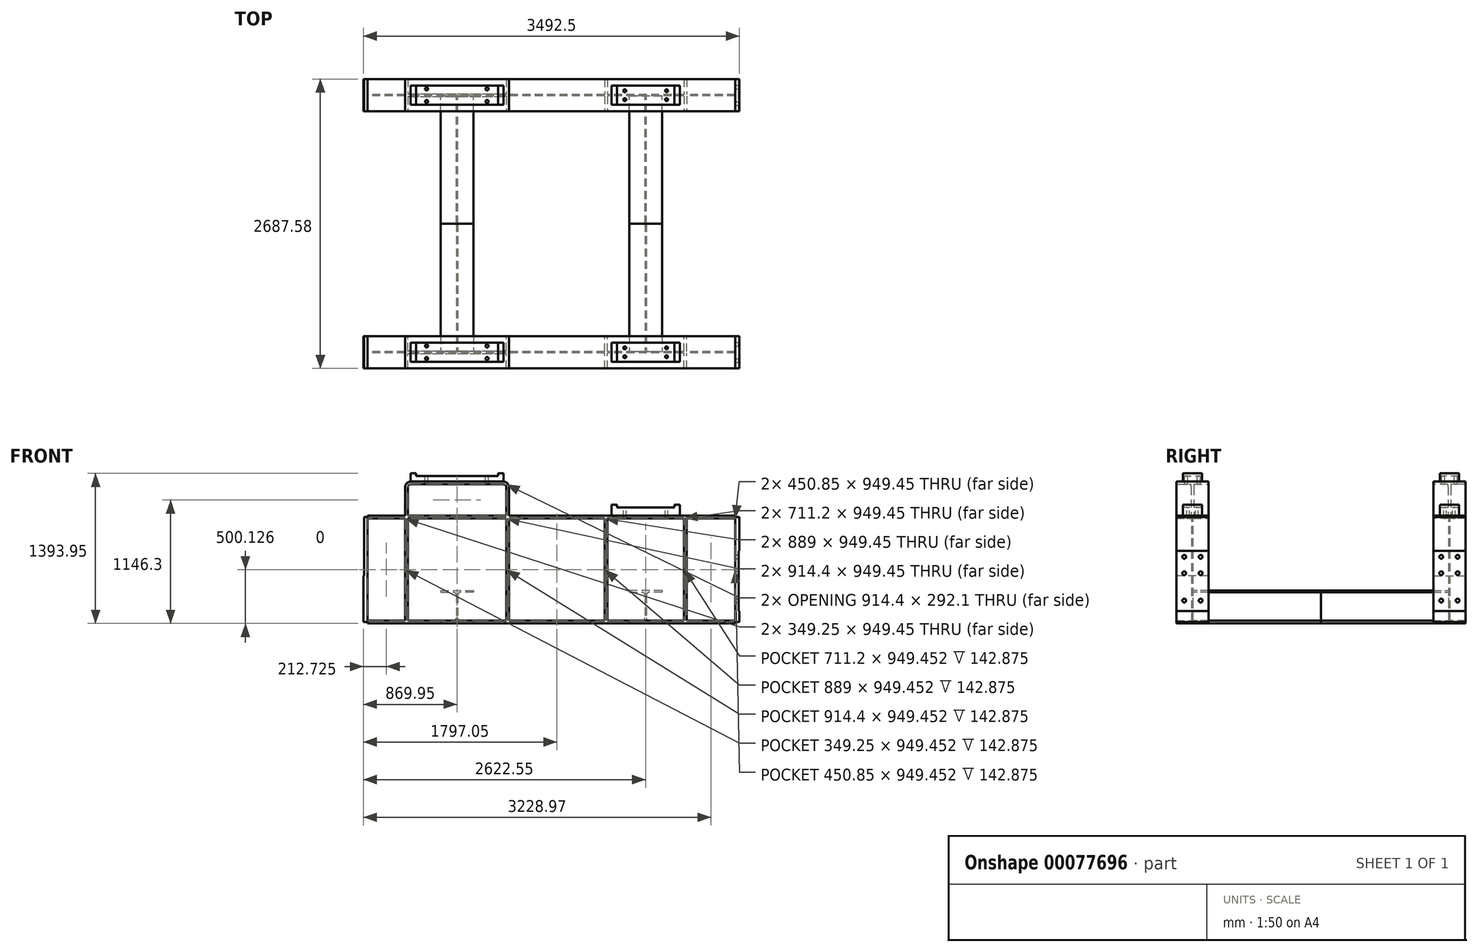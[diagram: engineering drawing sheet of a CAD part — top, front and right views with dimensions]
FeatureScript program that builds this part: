
annotation { "Feature Type Name" : "Feature", "Feature Type Description" : "" }
export const myFeature = defineFeature(function(context is Context, id is Id, definition is map)
    precondition{}
    {
        {
            var Q0;
            Q0=qCreatedBy(makeId("Front.planeOp"),FACE);
            var sketch = newSketch(context, id + "F0", { "sketchPlane" : qUnion([Q0])});
            skLineSegment(sketch, "E0.bottom", {"start": v(-1746.25, 0) * mm, "end": v(1746.25, 0) * mm});
            skLineSegment(sketch, "E0.top", {"start": v(-1746.25, 1000.25) * mm, "end": v(1746.25, 1000.25) * mm});
            skLineSegment(sketch, "E0.left", {"start": v(-1746.25, 0) * mm, "end": v(-1746.25, 1000.25) * mm});
            skLineSegment(sketch, "E0.right", {"start": v(1746.25, 0) * mm, "end": v(1746.25, 1000.25) * mm});
            skSolve(sketch);
        }
        {
            var Q0;
            Q0=qSketchRegion(id+"F0",true);
            extrude(context, id + "F1", {"entities" : qUnion([Q0]), "endBound" : BoundingType.SYMMETRIC, "depth" : 14.22 * mm});
        }
        {
            var Q0;
            Q0=qCreatedBy(makeId("Front.planeOp"),FACE);
            var sketch = newSketch(context, id + "F2", { "sketchPlane" : qUnion([Q0])});
            skLineSegment(sketch, "E1.bottom", {"start": v(-1708.15, 0) * mm, "end": v(1708.15, 0) * mm});
            skLineSegment(sketch, "E1.top", {"start": v(-1708.15, 25.4) * mm, "end": v(1708.15, 25.4) * mm});
            skLineSegment(sketch, "E1.left", {"start": v(-1708.15, 0) * mm, "end": v(-1708.15, 25.4) * mm});
            skLineSegment(sketch, "E1.right", {"start": v(1708.15, 0) * mm, "end": v(1708.15, 25.4) * mm});
            skLineSegment(sketch, "E2.0", {"start": v(1746.25, 0) * mm, "end": v(1746.25, 1000.25) * mm, "construction": true});
            skLineSegment(sketch, "E3.0", {"start": v(-1746.25, 0) * mm, "end": v(-1746.25, 1000.25) * mm, "construction": true});
            skLineSegment(sketch, "E4", {"start": v(-1746.25, 500.13) * mm, "end": v(1746.25, 500.13) * mm, "construction": true});
            skLineSegment(sketch, "E5.MirrorCS", {"start": v(1708.15, 1000.25) * mm, "end": v(1708.15, 974.85) * mm});
            skLineSegment(sketch, "E6.MirrorCS", {"start": v(-1708.15, 1000.25) * mm, "end": v(-1708.15, 974.85) * mm});
            skLineSegment(sketch, "E7.MirrorCS", {"start": v(-1708.15, 974.85) * mm, "end": v(1708.15, 974.85) * mm});
            skLineSegment(sketch, "E8.MirrorCS", {"start": v(-1708.15, 1000.25) * mm, "end": v(1708.15, 1000.25) * mm});
            skPoint(sketch, "E9.oppositeSnap0", {"position": v(-1708.15, 12.7) * mm});
            skLineSegment(sketch, "E9.bottom", {"start": v(-1708.15, 987.55) * mm, "end": v(-1746.25, 987.55) * mm});
            skLineSegment(sketch, "E9.top", {"start": v(-1708.15, 12.7) * mm, "end": v(-1746.25, 12.7) * mm});
            skLineSegment(sketch, "E9.left", {"start": v(-1708.15, 987.55) * mm, "end": v(-1708.15, 12.7) * mm});
            skLineSegment(sketch, "E9.right", {"start": v(-1746.25, 987.55) * mm, "end": v(-1746.25, 12.7) * mm});
            skLineSegment(sketch, "E10", {"start": v(0, 974.85) * mm, "end": v(0, 25.4) * mm, "construction": true});
            skLineSegment(sketch, "E11.MirrorCS", {"start": v(1708.15, 987.55) * mm, "end": v(1746.25, 987.55) * mm});
            skLineSegment(sketch, "E12.MirrorCS", {"start": v(1708.15, 12.7) * mm, "end": v(1746.25, 12.7) * mm});
            skLineSegment(sketch, "E13.MirrorCS", {"start": v(1746.25, 987.55) * mm, "end": v(1746.25, 12.7) * mm});
            skLineSegment(sketch, "E14.MirrorCS", {"start": v(1708.15, 987.55) * mm, "end": v(1708.15, 12.7) * mm});
            skPoint(sketch, "E15.MirrorP", {"position": v(1708.15, 12.7) * mm});
            skSolve(sketch);
        }
        {
            var Q0;
            Q0=qSketchRegion(id+"F2",true);
            extrude(context, id + "F3", {"entities" : qUnion([Q0]), "operationType" : NewBodyOperationType.ADD, "endBound" : BoundingType.SYMMETRIC, "depth" : 299.97 * mm});
        }
        {
            var Q0;
            Q0=qCreatedBy(makeId("Front.planeOp"),FACE);
            var sketch = newSketch(context, id + "F4", { "sketchPlane" : qUnion([Q0])});
            skPoint(sketch, "E16.0", {"position": v(-1746.25, 1000.25) * mm});
            skLineSegment(sketch, "E17.bottom", {"start": v(-1746.25, 1000.25) * mm, "end": v(-1739.9, 1000.25) * mm});
            skLineSegment(sketch, "E17.top", {"start": v(-1746.25, 441.45) * mm, "end": v(-1739.9, 441.45) * mm});
            skLineSegment(sketch, "E17.left", {"start": v(-1746.25, 1000.25) * mm, "end": v(-1746.25, 441.45) * mm});
            skLineSegment(sketch, "E17.right", {"start": v(-1739.9, 1000.25) * mm, "end": v(-1739.9, 441.45) * mm});
            skLineSegment(sketch, "E18", {"start": v(0, -58.3) * mm, "end": v(0, 1155.28) * mm, "construction": true});
            skLineSegment(sketch, "E19.MirrorCS", {"start": v(1746.25, 1000.25) * mm, "end": v(1739.9, 1000.25) * mm});
            skLineSegment(sketch, "E20.MirrorCS", {"start": v(1746.25, 441.45) * mm, "end": v(1739.9, 441.45) * mm});
            skPoint(sketch, "E21.MirrorP", {"position": v(1746.25, 1000.25) * mm});
            skLineSegment(sketch, "E22.bottom", {"start": v(1739.9, 441.45) * mm, "end": v(1766.35, 441.45) * mm});
            skLineSegment(sketch, "E22.top", {"start": v(1739.9, 114.3) * mm, "end": v(1766.35, 114.3) * mm});
            skLineSegment(sketch, "E22.left", {"start": v(1739.9, 441.45) * mm, "end": v(1739.9, 114.3) * mm});
            skLineSegment(sketch, "E22.right", {"start": v(1766.35, 441.45) * mm, "end": v(1766.35, 114.3) * mm});
            skLineSegment(sketch, "E23.top", {"start": v(1739.9, 673.1) * mm, "end": v(1766.35, 673.1) * mm});
            skLineSegment(sketch, "E23.left", {"start": v(1739.9, 441.45) * mm, "end": v(1739.9, 673.1) * mm});
            skLineSegment(sketch, "E23.right", {"start": v(1766.35, 441.45) * mm, "end": v(1766.35, 673.1) * mm});
            skSolve(sketch);
        }
        {
            var Q0;
            Q0=qSketchRegion(id+"F4",true);
            extrude(context, id + "F5", {"entities" : qUnion([Q0]), "operationType" : NewBodyOperationType.REMOVE, "endBound" : BoundingType.SYMMETRIC, "oppositeDirection" : true, "depth" : 304.8 * mm});
        }
        {
            var Q0;
            Q0=makeQuery(id+"F3.opExtrude","CAP_FACE",FACE,{"disambiguationData":[OSD([sQuery(id+"F2.wireOp",EDGE,"E1.bottom"),sQuery(id+"F2.wireOp",EDGE,"E1.top"),sQuery(id+"F2.wireOp",EDGE,"E1.left"),sQuery(id+"F2.wireOp",EDGE,"E6.MirrorCS"),sQuery(id+"F2.wireOp",EDGE,"E7.MirrorCS"),sQuery(id+"F2.wireOp",EDGE,"E8.MirrorCS"),sQuery(id+"F2.wireOp",EDGE,"E9.bottom"),sQuery(id+"F2.wireOp",EDGE,"E9.top"),sQuery(id+"F2.wireOp",EDGE,"E9.left"),sQuery(id+"F2.wireOp",EDGE,"E9.right"),sQuery(id+"F2.wireOp",EDGE,"E5.MirrorCS"),sQuery(id+"F2.wireOp",EDGE,"E1.right"),sQuery(id+"F2.wireOp",EDGE,"E11.MirrorCS"),sQuery(id+"F2.wireOp",EDGE,"E12.MirrorCS"),sQuery(id+"F2.wireOp",EDGE,"E13.MirrorCS"),sQuery(id+"F2.wireOp",EDGE,"E14.MirrorCS")])],"isStart":false});
            var sketch = newSketch(context, id + "F6", { "sketchPlane" : qUnion([Q0])});
            skLineSegment(sketch, "E24.bottom", {"start": v(-1708.15, 987.55) * mm, "end": v(-1777.82, 987.55) * mm});
            skLineSegment(sketch, "E24.top", {"start": v(-1708.15, 1019.74) * mm, "end": v(-1777.82, 1019.74) * mm});
            skLineSegment(sketch, "E24.left", {"start": v(-1708.15, 987.55) * mm, "end": v(-1708.15, 1019.74) * mm});
            skLineSegment(sketch, "E24.right", {"start": v(-1777.82, 987.55) * mm, "end": v(-1777.82, 1019.74) * mm});
            skLineSegment(sketch, "E25.bottom", {"start": v(1708.15, 987.55) * mm, "end": v(1769.2, 987.55) * mm});
            skLineSegment(sketch, "E25.top", {"start": v(1708.15, 1033.96) * mm, "end": v(1769.2, 1033.96) * mm});
            skLineSegment(sketch, "E25.left", {"start": v(1708.15, 987.55) * mm, "end": v(1708.15, 1033.96) * mm});
            skLineSegment(sketch, "E25.right", {"start": v(1769.2, 987.55) * mm, "end": v(1769.2, 1033.96) * mm});
            skLineSegment(sketch, "E26.bottom", {"start": v(1708.15, 12.7) * mm, "end": v(1775.25, 12.7) * mm});
            skLineSegment(sketch, "E26.top", {"start": v(1708.15, -29.13) * mm, "end": v(1775.25, -29.13) * mm});
            skLineSegment(sketch, "E26.left", {"start": v(1708.15, 12.7) * mm, "end": v(1708.15, -29.13) * mm});
            skLineSegment(sketch, "E26.right", {"start": v(1775.25, 12.7) * mm, "end": v(1775.25, -29.13) * mm});
            skLineSegment(sketch, "E27.bottom", {"start": v(-1708.15, 12.7) * mm, "end": v(-1780.9, 12.7) * mm});
            skLineSegment(sketch, "E27.top", {"start": v(-1708.15, -36.57) * mm, "end": v(-1780.9, -36.57) * mm});
            skLineSegment(sketch, "E27.left", {"start": v(-1708.15, 12.7) * mm, "end": v(-1708.15, -36.57) * mm});
            skLineSegment(sketch, "E27.right", {"start": v(-1780.9, 12.7) * mm, "end": v(-1780.9, -36.57) * mm});
            skSolve(sketch);
        }
        {
            var Q0;
            Q0=qSketchRegion(id+"F6",true);
            extrude(context, id + "F7", {"entities" : qUnion([Q0]), "operationType" : NewBodyOperationType.REMOVE, "endBound" : BoundingType.THROUGH_ALL, "oppositeDirection" : true, "depth" : 25.4 * mm});
        }
        {
            var Q0;
            Q0=qCreatedBy(makeId("Front.planeOp"),FACE);
            var sketch = newSketch(context, id + "F8", { "sketchPlane" : qUnion([Q0])});
            skLineSegment(sketch, "E28.0", {"start": v(-876.3, 987.55) * mm, "end": v(-876.3, 441.45) * mm, "construction": true});
            skLineSegment(sketch, "E29.0", {"start": v(876.3, 987.55) * mm, "end": v(876.3, 441.45) * mm, "construction": true});
            skLineSegment(sketch, "E30.0", {"start": v(-1708.15, 25.4) * mm, "end": v(1708.15, 25.4) * mm});
            skLineSegment(sketch, "E31.0", {"start": v(-1333.5, 1317.75) * mm, "end": v(-1333.5, 25.4) * mm});
            skLineSegment(sketch, "E32.0", {"start": v(-1358.9, 1266.95) * mm, "end": v(-1358.9, 25.4) * mm});
            skLineSegment(sketch, "E33.0", {"start": v(-1308.1, 1317.75) * mm, "end": v(-444.5, 1317.75) * mm});
            skLineSegment(sketch, "E34.0", {"start": v(-1308.1, 1292.35) * mm, "end": v(-444.5, 1292.35) * mm});
            skLineSegment(sketch, "E34.1", {"start": v(-1333.5, 1266.95) * mm, "end": v(-1333.5, 25.4) * mm});
            skLineSegment(sketch, "E35.MirrorCS", {"start": v(-419.1, 1266.95) * mm, "end": v(-419.1, 25.4) * mm});
            skLineSegment(sketch, "E36.MirrorCS", {"start": v(-393.7, 1266.95) * mm, "end": v(-393.7, 25.4) * mm});
            skLineSegment(sketch, "E37.MirrorCS", {"start": v(-419.1, 1292.35) * mm, "end": v(-419.1, 25.4) * mm});
            skPoint(sketch, "E38.visualSharp", {"position": v(-1333.5, 1292.35) * mm});
            skArc(sketch, "E38.filletArc", {"start": v(-1308.1, 1292.35) * mm, "mid": v(-1326.06, 1284.91) * mm, "end": v(-1333.5, 1266.95) * mm});
            skPoint(sketch, "E39.newPointB", {"position": v(-419.1, 1317.75) * mm});
            skArc(sketch, "E39.filletArc", {"start": v(-419.1, 1266.95) * mm, "mid": v(-426.54, 1284.91) * mm, "end": v(-444.5, 1292.35) * mm});
            skPoint(sketch, "E40.visualSharp", {"position": v(-1358.9, 1317.75) * mm});
            skArc(sketch, "E40.filletArc", {"start": v(-1308.1, 1317.75) * mm, "mid": v(-1344.02, 1302.87) * mm, "end": v(-1358.9, 1266.95) * mm});
            skPoint(sketch, "E41.visualSharp", {"position": v(-393.7, 1317.75) * mm});
            skArc(sketch, "E41.filletArc", {"start": v(-393.7, 1266.95) * mm, "mid": v(-408.58, 1302.87) * mm, "end": v(-444.5, 1317.75) * mm});
            skLineSegment(sketch, "E42", {"start": v(0, 1077.49) * mm, "end": v(0, -160.54) * mm, "construction": true});
            skLineSegment(sketch, "E43.0", {"start": v(-1708.15, 974.85) * mm, "end": v(1708.15, 974.85) * mm});
            skLineSegment(sketch, "E44.0.1", {"start": v(1708.15, 25.4) * mm, "end": v(1708.15, 974.85) * mm});
            skLineSegment(sketch, "E44.0.2", {"start": v(1708.15, 974.85) * mm, "end": v(-1708.15, 974.85) * mm});
            skLineSegment(sketch, "E44.0.3", {"start": v(-1708.15, 974.85) * mm, "end": v(-1708.15, 25.4) * mm});
            skLineSegment(sketch, "E45.0", {"start": v(520.7, 974.85) * mm, "end": v(520.7, 25.4) * mm});
            skLineSegment(sketch, "E46.0", {"start": v(495.3, 974.85) * mm, "end": v(495.3, 25.4) * mm});
            skLineSegment(sketch, "E47.MirrorCS", {"start": v(1231.9, 974.85) * mm, "end": v(1231.9, 25.4) * mm});
            skLineSegment(sketch, "E48.MirrorCS", {"start": v(1257.3, 974.85) * mm, "end": v(1257.3, 25.4) * mm});
            skSolve(sketch);
        }
        {
            var Q0;
            Q0=makeQuery(id+"F8.imprint","IMPRINT",FACE,{"disambiguationData":[TD([[makeQuery(id+"F8.imprint","IMPRINT",EDGE,{"derivedFrom":sQuery(id+"F8.wireOp",EDGE,"E34.0")}),-1.0]])]});
            extrude(context, id + "F9", {"entities" : qUnion([Q0]), "operationType" : NewBodyOperationType.ADD, "endBound" : BoundingType.SYMMETRIC, "depth" : 25.4 * mm});
        }
        {
            var Q0;
            {var subQ0=sQuery(id+"F8.wireOp",EDGE,"E40.filletArc");var subQ1=sQuery(id+"F8.wireOp",EDGE,"E32.0");var subQ2=makeQuery(id+"F8.imprint","INTERSECT",VERTEX,{"derivedFrom":[subQ1,subQ0]});Q0=makeQuery(id+"F8.imprint","IMPRINT",FACE,{"disambiguationData":[TD([[makeQuery(id+"F8.imprint","IMPRINT",EDGE,{"disambiguationData":[TD([[subQ2,-1.0]])],"derivedFrom":subQ1}),1.0]])]});}
            var Q1;
            {var subQ7=sQuery(id+"F8.wireOp",EDGE,"E33.0");Q1=makeQuery(id+"F8.imprint","IMPRINT",FACE,{"disambiguationData":[TD([[makeQuery(id+"F8.imprint","IMPRINT",EDGE,{"derivedFrom":subQ7}),-1.0]])]});}
            extrude(context, id + "F10", {"entities" : qUnion([Q0, Q1]), "operationType" : NewBodyOperationType.ADD, "endBound" : BoundingType.SYMMETRIC, "depth" : 299.97 * mm});
        }
        {
            var Q0;
            {var subQ0=sQuery(id+"F8.wireOp",EDGE,"E30.0");var subQ1=sQuery(id+"F8.wireOp",EDGE,"E32.0");var subQ2=makeQuery(id+"F8.imprint","INTERSECT",VERTEX,{"derivedFrom":[subQ1,subQ0]});Q0=makeQuery(id+"F8.imprint","IMPRINT",FACE,{"disambiguationData":[TD([[makeQuery(id+"F8.imprint","IMPRINT",EDGE,{"disambiguationData":[TD([[subQ2,1.0]])],"derivedFrom":subQ1}),1.0]])]});}
            var Q1;
            {var subQ0=sQuery(id+"F8.wireOp",EDGE,"E30.0");var subQ1=sQuery(id+"F8.wireOp",EDGE,"E36.MirrorCS");var subQ2=makeQuery(id+"F8.imprint","INTERSECT",VERTEX,{"derivedFrom":[subQ1,subQ0]});Q1=makeQuery(id+"F8.imprint","IMPRINT",FACE,{"disambiguationData":[TD([[makeQuery(id+"F8.imprint","IMPRINT",EDGE,{"disambiguationData":[TD([[subQ2,1.0]])],"derivedFrom":subQ1}),-1.0]])]});}
            var Q2;
            {var subQ0=sQuery(id+"F8.wireOp",EDGE,"E45.0");Q2=makeQuery(id+"F8.imprint","IMPRINT",FACE,{"disambiguationData":[TD([[makeQuery(id+"F8.imprint","IMPRINT",EDGE,{"derivedFrom":subQ0}),-1.0]])]});}
            var Q3;
            {var subQ0=sQuery(id+"F8.wireOp",EDGE,"E47.MirrorCS");Q3=makeQuery(id+"F8.imprint","IMPRINT",FACE,{"disambiguationData":[TD([[makeQuery(id+"F8.imprint","IMPRINT",EDGE,{"derivedFrom":subQ0}),1.0]])]});}
            extrude(context, id + "F11", {"entities" : qUnion([Q0, Q1, Q2, Q3]), "endBound" : BoundingType.SYMMETRIC, "depth" : 299.97 * mm});
        }
        {
            var Q0;
            Q0=makeQuery(id+"F1.opExtrude","SWEPT_BODY",BODY,{"disambiguationData":[OSD([sQuery(id+"F0.wireOp",EDGE,"E0.bottom"),sQuery(id+"F0.wireOp",EDGE,"E0.top"),sQuery(id+"F0.wireOp",EDGE,"E0.left"),sQuery(id+"F0.wireOp",EDGE,"E0.right")])]});
            var Q1;
            Q1=makeQuery(id+"F11.opExtrude","SWEPT_BODY",BODY,{"disambiguationData":[OSD([sQuery(id+"F8.wireOp",EDGE,"E32.0"),sQuery(id+"F8.wireOp",EDGE,"E34.1"),sQuery(id+"F8.wireOp",EDGE,"E30.0"),sQuery(id+"F8.wireOp",EDGE,"E44.0.2")])]});
            var Q2;
            Q2=makeQuery(id+"F11.opExtrude","SWEPT_BODY",BODY,{"disambiguationData":[OSD([sQuery(id+"F8.wireOp",EDGE,"E36.MirrorCS"),sQuery(id+"F8.wireOp",EDGE,"E37.MirrorCS"),sQuery(id+"F8.wireOp",EDGE,"E30.0"),sQuery(id+"F8.wireOp",EDGE,"E44.0.2")])]});
            var Q3;
            Q3=makeQuery(id+"F11.opExtrude","SWEPT_BODY",BODY,{"disambiguationData":[OSD([sQuery(id+"F8.wireOp",EDGE,"E30.0"),sQuery(id+"F8.wireOp",EDGE,"E44.0.2"),sQuery(id+"F8.wireOp",EDGE,"E45.0"),sQuery(id+"F8.wireOp",EDGE,"E46.0")])]});
            var Q4;
            Q4=makeQuery(id+"F11.opExtrude","SWEPT_BODY",BODY,{"disambiguationData":[OSD([sQuery(id+"F8.wireOp",EDGE,"E30.0"),sQuery(id+"F8.wireOp",EDGE,"E44.0.2"),sQuery(id+"F8.wireOp",EDGE,"E47.MirrorCS"),sQuery(id+"F8.wireOp",EDGE,"E48.MirrorCS")])]});
            booleanBodies(context, id + "F12", {"operationType" : BooleanOperationType.UNION, "tools" : qUnion([Q0, Q1, Q2, Q3, Q4])});
        }
        {
            var Q0;
            {var subQ11=sQuery(id+"F2.wireOp",EDGE,"E5.MirrorCS");var subQ21=sQuery(id+"F2.wireOp",EDGE,"E8.MirrorCS");Q0=makeQuery(id+"F10.boolean.opBoolean","SPLIT",FACE,{"disambiguationData":[TD([makeQuery(id+"F3.opExtrude","SWEPT_FACE",FACE,{"disambiguationData":[OSD([subQ11])]})])],"derivedFrom":makeQuery(id+"F3.boolean.opBoolean","MERGE",FACE,{"derivedFrom":[makeQuery(id+"F1.opExtrude","SWEPT_FACE",FACE,{"disambiguationData":[OSD([sQuery(id+"F0.wireOp",EDGE,"E0.top")])]}),makeQuery(id+"F3.opExtrude","SWEPT_FACE",FACE,{"disambiguationData":[OSD([subQ21])]})]})});}
            var sketch = newSketch(context, id + "F13", { "sketchPlane" : qUnion([Q0])});
            skLineSegment(sketch, "E49.0", {"start": v(1739.9, 149.99) * mm, "end": v(1739.9, -149.99) * mm, "construction": true});
            skLineSegment(sketch, "E50.0", {"start": v(876.3, 149.99) * mm, "end": v(876.3, -149.99) * mm, "construction": true});
            skLineSegment(sketch, "E51", {"start": v(1921.42, 0) * mm, "end": v(-99.23, 0) * mm, "construction": true});
            skPoint(sketch, "E51.endSnap0", {"position": v(1708.15, 0) * mm});
            skLineSegment(sketch, "E52.0", {"start": v(1193.8, 88.9) * mm, "end": v(1193.8, -88.9) * mm});
            skLineSegment(sketch, "E53.0", {"start": v(558.8, 88.9) * mm, "end": v(558.8, -88.9) * mm});
            skLineSegment(sketch, "E54.0", {"start": v(1193.8, 88.9) * mm, "end": v(558.8, 88.9) * mm});
            skLineSegment(sketch, "E55.trimOffspring", {"start": v(1193.8, -88.9) * mm, "end": v(558.8, -88.9) * mm});
            skSolve(sketch);
        }
        {
            var Q0;
            Q0 = qSketchRegion(id + "F13", true);
            extrude(context, id + "F14", {"entities" : qUnion([Q0]), "operationType" : NewBodyOperationType.ADD, "depth" : 76.2 * mm});
        }
        {
            var Q0;
            Q0=makeQuery(id+"F14.opExtrude","CAP_FACE",FACE,{"disambiguationData":[OSD([sQuery(id+"F13.wireOp",EDGE,"E52.0"),sQuery(id+"F13.wireOp",EDGE,"E53.0"),sQuery(id+"F13.wireOp",EDGE,"E54.0"),sQuery(id+"F13.wireOp",EDGE,"E55.trimOffspring")])],"isStart":false});
            var sketch = newSketch(context, id + "F15", { "sketchPlane" : qUnion([Q0])});
            skLineSegment(sketch, "E56", {"start": v(876.3, 88.9) * mm, "end": v(876.3, -88.9) * mm, "construction": true});
            skLineSegment(sketch, "E57.0", {"start": v(1143, 88.9) * mm, "end": v(1143, -88.9) * mm, "construction": true});
            skLineSegment(sketch, "E58.bottom", {"start": v(1143, 88.9) * mm, "end": v(1193.8, 88.9) * mm});
            skLineSegment(sketch, "E58.top", {"start": v(1143, -88.9) * mm, "end": v(1193.8, -88.9) * mm});
            skLineSegment(sketch, "E58.left", {"start": v(1143, 88.9) * mm, "end": v(1143, -88.9) * mm});
            skLineSegment(sketch, "E58.right", {"start": v(1193.8, 88.9) * mm, "end": v(1193.8, -88.9) * mm});
            skLineSegment(sketch, "E59.MirrorCS", {"start": v(609.6, 88.9) * mm, "end": v(609.6, -88.9) * mm, "construction": true});
            skLineSegment(sketch, "E60.MirrorCS", {"start": v(558.8, 88.9) * mm, "end": v(558.8, -88.9) * mm});
            skLineSegment(sketch, "E61.MirrorCS", {"start": v(609.6, 88.9) * mm, "end": v(609.6, -88.9) * mm});
            skLineSegment(sketch, "E62.MirrorCS", {"start": v(609.6, -88.9) * mm, "end": v(558.8, -88.9) * mm});
            skLineSegment(sketch, "E63.MirrorCS", {"start": v(609.6, 88.9) * mm, "end": v(558.8, 88.9) * mm});
            skSolve(sketch);
        }
        {
            var Q0;
            Q0 = qSketchRegion(id + "F15", true);
            extrude(context, id + "F16", {"entities" : qUnion([Q0]), "operationType" : NewBodyOperationType.ADD, "depth" : 25.4 * mm});
        }
        {
            var Q0;
            Q0=makeQuery(id+"F14.opExtrude","CAP_FACE",FACE,{"disambiguationData":[OSD([sQuery(id+"F13.wireOp",EDGE,"E52.0"),sQuery(id+"F13.wireOp",EDGE,"E53.0"),sQuery(id+"F13.wireOp",EDGE,"E54.0"),sQuery(id+"F13.wireOp",EDGE,"E55.trimOffspring")])],"isStart":false});
            var sketch = newSketch(context, id + "F17", { "sketchPlane" : qUnion([Q0])});
            skLineSegment(sketch, "E64", {"start": v(876.3, 88.9) * mm, "end": v(876.3, -88.9) * mm, "construction": true});
            skLineSegment(sketch, "E65", {"start": v(609.6, 0) * mm, "end": v(1143, 0) * mm, "construction": true});
            skLineSegment(sketch, "E66.0", {"start": v(1070.86, 88.9) * mm, "end": v(1070.86, -88.9) * mm, "construction": true});
            skLineSegment(sketch, "E67.0", {"start": v(609.6, 41.15) * mm, "end": v(1143, 41.15) * mm, "construction": true});
            skLineSegment(sketch, "E68.0", {"start": v(609.6, -41.15) * mm, "end": v(1143, -41.15) * mm, "construction": true});
            skLineSegment(sketch, "E69.0", {"start": v(682, 88.9) * mm, "end": v(682, -88.9) * mm, "construction": true});
            skPoint(sketch, "E70", {"position": v(682, 41.15) * mm});
            skPoint(sketch, "E71", {"position": v(682, -41.15) * mm});
            skPoint(sketch, "E72", {"position": v(1070.86, 41.15) * mm});
            skPoint(sketch, "E73", {"position": v(1070.86, -41.15) * mm});
            skSolve(sketch);
        }
        {
            var Q0;
            Q0=sQuery(id+"F17.wireOp",VERTEX,"E70");
            var Q1;
            Q1=sQuery(id+"F17.wireOp",VERTEX,"E72");
            var Q2;
            Q2=sQuery(id+"F17.wireOp",VERTEX,"E73");
            var Q3;
            Q3=sQuery(id+"F17.wireOp",VERTEX,"E71");
            var Q4;
            Q4=makeQuery(id+"F1.opExtrude","SWEPT_BODY",BODY,{"disambiguationData":[OSD([sQuery(id+"F0.wireOp",EDGE,"E0.bottom"),sQuery(id+"F0.wireOp",EDGE,"E0.top"),sQuery(id+"F0.wireOp",EDGE,"E0.left"),sQuery(id+"F0.wireOp",EDGE,"E0.right")])]});
            hole(context, id + "F18", {"style" : HoleStyle.SIMPLE, "endStyle" : HoleEndStyle.BLIND, "standardTappedOrClearance" : lookupTablePath({ "standard" : "ANSI", "fit" : "Normal (ASME)", "size" : "1", "type" : "Clearance" }), "standardBlindInLast" : lookupTablePath({ "fit" : "Free", "standard" : "ANSI", "size" : "1", "type" : "Clearance" }), "holeDiameter" : 26.2 * mm, "holeDepth" : 101.6 * mm, "locations" : qUnion([Q0, Q1, Q2, Q3]), "scope" : qUnion([Q4])});
        }
        {
            var Q0;
            Q0=makeQuery(id+"F5.boolean.opBoolean","COPY",FACE,{"derivedFrom":makeQuery(id+"F5.opExtrude","SWEPT_FACE",FACE,{"disambiguationData":[OSD([sQuery(id+"F4.wireOp",EDGE,"E22.left"),sQuery(id+"F4.wireOp",EDGE,"E23.left")])]})});
            var sketch = newSketch(context, id + "F19", { "sketchPlane" : qUnion([Q0])});
            skLineSegment(sketch, "E74.0", {"start": v(88.9, 1076.45) * mm, "end": v(-88.9, 1076.45) * mm, "construction": true});
            skLineSegment(sketch, "E75.0", {"start": v(88.9, 619.25) * mm, "end": v(-88.9, 619.25) * mm, "construction": true});
            skLineSegment(sketch, "E76.0", {"start": v(88.9, 466.85) * mm, "end": v(-88.9, 466.85) * mm, "construction": true});
            skLineSegment(sketch, "E77.0", {"start": v(88.9, 212.85) * mm, "end": v(-88.9, 212.85) * mm, "construction": true});
            skLineSegment(sketch, "E78", {"start": v(0, -74.03) * mm, "end": v(0, 756.57) * mm, "construction": true});
            skPoint(sketch, "E78.endSnap0", {"position": v(0, 673.1) * mm});
            skLineSegment(sketch, "E79.0", {"start": v(-76.2, -74.03) * mm, "end": v(-76.2, 756.57) * mm, "construction": true});
            skPoint(sketch, "E80", {"position": v(-76.2, 619.25) * mm});
            skPoint(sketch, "E81", {"position": v(-76.2, 466.85) * mm});
            skPoint(sketch, "E82", {"position": v(-76.2, 212.85) * mm});
            skPoint(sketch, "E83.MirrorP", {"position": v(76.2, 619.25) * mm});
            skPoint(sketch, "E84.MirrorP", {"position": v(76.2, 466.85) * mm});
            skPoint(sketch, "E85.MirrorP", {"position": v(76.2, 212.85) * mm});
            skSolve(sketch);
        }
        {
            var Q0;
            Q0=sQuery(id+"F19.wireOp",VERTEX,"E80");
            var Q1;
            Q1=sQuery(id+"F19.wireOp",VERTEX,"E83.MirrorP");
            var Q2;
            Q2=sQuery(id+"F19.wireOp",VERTEX,"E84.MirrorP");
            var Q3;
            Q3=sQuery(id+"F19.wireOp",VERTEX,"E81");
            var Q4;
            Q4=sQuery(id+"F19.wireOp",VERTEX,"E85.MirrorP");
            var Q5;
            Q5=sQuery(id+"F19.wireOp",VERTEX,"E82");
            var Q6;
            Q6=makeQuery(id+"F1.opExtrude","SWEPT_BODY",BODY,{"disambiguationData":[OSD([sQuery(id+"F0.wireOp",EDGE,"E0.bottom"),sQuery(id+"F0.wireOp",EDGE,"E0.top"),sQuery(id+"F0.wireOp",EDGE,"E0.left"),sQuery(id+"F0.wireOp",EDGE,"E0.right")])]});
            hole(context, id + "F20", {"style" : HoleStyle.SIMPLE, "endStyle" : HoleEndStyle.BLIND, "holeDiameter" : 35.05 * mm, "holeDepth" : 101.6 * mm, "locations" : qUnion([Q0, Q1, Q2, Q3, Q4, Q5]), "scope" : qUnion([Q6])});
        }
        {
            var Q0;
            Q0=makeQuery(id+"F10.opExtrude","SWEPT_FACE",FACE,{"disambiguationData":[OSD([sQuery(id+"F8.wireOp",EDGE,"E33.0")])]});
            var sketch = newSketch(context, id + "F21", { "sketchPlane" : qUnion([Q0])});
            skLineSegment(sketch, "E86.0", {"start": v(1143, 88.9) * mm, "end": v(609.6, 88.9) * mm, "construction": true});
            skLineSegment(sketch, "E87", {"start": v(876.3, 88.9) * mm, "end": v(876.3, -517.5) * mm, "construction": true});
            skLineSegment(sketch, "E88.0", {"start": v(-876.3, 88.9) * mm, "end": v(-876.3, -517.5) * mm, "construction": true});
            skLineSegment(sketch, "E89", {"start": v(-1945.55, 0) * mm, "end": v(-145.35, 0) * mm, "construction": true});
            skLineSegment(sketch, "E90.0", {"start": v(-1308.1, 88.9) * mm, "end": v(-1308.1, -517.5) * mm, "construction": true});
            skLineSegment(sketch, "E91.0", {"start": v(-1945.55, -88.9) * mm, "end": v(-145.35, -88.9) * mm, "construction": true});
            skLineSegment(sketch, "E92.bottom", {"start": v(-1308.1, -88.9) * mm, "end": v(-444.5, -88.9) * mm});
            skLineSegment(sketch, "E92.top", {"start": v(-1308.1, 88.9) * mm, "end": v(-444.5, 88.9) * mm});
            skLineSegment(sketch, "E92.left", {"start": v(-1308.1, -88.9) * mm, "end": v(-1308.1, 88.9) * mm});
            skLineSegment(sketch, "E92.right", {"start": v(-444.5, -88.9) * mm, "end": v(-444.5, 88.9) * mm});
            skSolve(sketch);
        }
        {
            var Q0;
            Q0 = qSketchRegion(id + "F21", true);
            extrude(context, id + "F22", {"entities" : qUnion([Q0]), "operationType" : NewBodyOperationType.ADD, "depth" : 76.2 * mm});
        }
        {
            var Q0;
            Q0=makeQuery(id+"F22.opExtrude","CAP_FACE",FACE,{"disambiguationData":[OSD([sQuery(id+"F21.wireOp",EDGE,"E92.bottom"),sQuery(id+"F21.wireOp",EDGE,"E92.top"),sQuery(id+"F21.wireOp",EDGE,"E92.left"),sQuery(id+"F21.wireOp",EDGE,"E92.right")])],"isStart":false});
            var sketch = newSketch(context, id + "F23", { "sketchPlane" : qUnion([Q0])});
            skLineSegment(sketch, "E93.0", {"start": v(-495.3, -88.9) * mm, "end": v(-495.3, 88.9) * mm});
            skLineSegment(sketch, "E94.0", {"start": v(-1257.3, -88.9) * mm, "end": v(-1257.3, 88.9) * mm});
            skLineSegment(sketch, "E95.0", {"start": v(-1308.1, 88.9) * mm, "end": v(-444.5, 88.9) * mm});
            skLineSegment(sketch, "E96.0", {"start": v(-1308.1, -88.9) * mm, "end": v(-444.5, -88.9) * mm});
            skSolve(sketch);
        }
        {
            var Q0;
            Q0 = qSketchRegion(id + "F23", true);
            extrude(context, id + "F24", {"entities" : qUnion([Q0]), "operationType" : NewBodyOperationType.REMOVE, "oppositeDirection" : true, "depth" : 25.4 * mm});
        }
        {
            var Q0;
            Q0=makeQuery(id+"F24.boolean.opBoolean","COPY",FACE,{"derivedFrom":makeQuery(id+"F24.opExtrude","CAP_FACE",FACE,{"disambiguationData":[OSD([sQuery(id+"F23.wireOp",EDGE,"E93.0"),sQuery(id+"F23.wireOp",EDGE,"E94.0"),sQuery(id+"F23.wireOp",EDGE,"E95.0"),sQuery(id+"F23.wireOp",EDGE,"E96.0")])],"isStart":false})});
            var sketch = newSketch(context, id + "F25", { "sketchPlane" : qUnion([Q0])});
            skLineSegment(sketch, "E97", {"start": v(-495.3, 0) * mm, "end": v(-1257.3, 0) * mm, "construction": true});
            skLineSegment(sketch, "E98", {"start": v(-876.3, 88.9) * mm, "end": v(-876.3, -88.9) * mm, "construction": true});
            skLineSegment(sketch, "E99.0", {"start": v(-495.3, 58.67) * mm, "end": v(-1257.3, 58.67) * mm, "construction": true});
            skLineSegment(sketch, "E100.0", {"start": v(-1158.75, 88.9) * mm, "end": v(-1158.75, -88.9) * mm, "construction": true});
            skLineSegment(sketch, "E101.0", {"start": v(-596.9, 88.9) * mm, "end": v(-596.9, -88.9) * mm, "construction": true});
            skPoint(sketch, "E102", {"position": v(-1158.75, 58.67) * mm});
            skPoint(sketch, "E103", {"position": v(-596.9, 58.67) * mm});
            skPoint(sketch, "E104.MirrorP", {"position": v(-1158.75, -58.67) * mm});
            skPoint(sketch, "E105.MirrorP", {"position": v(-596.9, -58.67) * mm});
            skSolve(sketch);
        }
        {
            var Q0;
            Q0=sQuery(id+"F25.wireOp",VERTEX,"E102");
            var Q1;
            Q1=sQuery(id+"F25.wireOp",VERTEX,"E104.MirrorP");
            var Q2;
            Q2=sQuery(id+"F25.wireOp",VERTEX,"E103");
            var Q3;
            Q3=sQuery(id+"F25.wireOp",VERTEX,"E105.MirrorP");
            var Q4;
            Q4=makeQuery(id+"F1.opExtrude","SWEPT_BODY",BODY,{"disambiguationData":[OSD([sQuery(id+"F0.wireOp",EDGE,"E0.bottom"),sQuery(id+"F0.wireOp",EDGE,"E0.top"),sQuery(id+"F0.wireOp",EDGE,"E0.left"),sQuery(id+"F0.wireOp",EDGE,"E0.right")])]});
            hole(context, id + "F26", {"style" : HoleStyle.SIMPLE, "endStyle" : HoleEndStyle.BLIND, "holeDiameter" : 28.57 * mm, "holeDepth" : 101.6 * mm, "locations" : qUnion([Q0, Q1, Q2, Q3]), "scope" : qUnion([Q4])});
        }
        {
            var Q0;
            {var subQ0=makeQuery(id+"F3.opExtrude","SWEPT_FACE",FACE,{"disambiguationData":[OSD([sQuery(id+"F2.wireOp",EDGE,"E1.top")])]});Q0=makeQuery(id+"F12.opBoolean","SPLIT",FACE,{"disambiguationData":[TD([makeQuery(id+"F11.opExtrude","SWEPT_FACE",FACE,{"disambiguationData":[OSD([sQuery(id+"F8.wireOp",EDGE,"E45.0")])]})])],"derivedFrom":makeQuery(id+"F3.boolean.opBoolean","SPLIT",FACE,{"disambiguationData":[TD([subQ0])],"derivedFrom":makeQuery(id+"F1.opExtrude","CAP_FACE",FACE,{"disambiguationData":[OSD([sQuery(id+"F0.wireOp",EDGE,"E0.bottom"),sQuery(id+"F0.wireOp",EDGE,"E0.top"),sQuery(id+"F0.wireOp",EDGE,"E0.left"),sQuery(id+"F0.wireOp",EDGE,"E0.right")])],"isStart":true})})});}
            var sketch = newSketch(context, id + "F27", { "sketchPlane" : qUnion([Q0])});
            skLineSegment(sketch, "E106.0", {"start": v(-1143, 1076.45) * mm, "end": v(-609.6, 1076.45) * mm, "construction": true});
            skLineSegment(sketch, "E107.0", {"start": v(1257.3, 1368.55) * mm, "end": v(495.3, 1368.55) * mm, "construction": true});
            skLineSegment(sketch, "E108", {"start": v(-876.3, 1076.45) * mm, "end": v(-876.3, 0) * mm, "construction": true});
            skPoint(sketch, "E108.endSnap0", {"position": v(-876.3, 25.4) * mm});
            skLineSegment(sketch, "E109", {"start": v(876.3, 1368.55) * mm, "end": v(876.3, 0) * mm, "construction": true});
            skPoint(sketch, "E109.endSnap0", {"position": v(876.3, 1368.55) * mm});
            skLineSegment(sketch, "E110.0", {"start": v(1708.15, 0) * mm, "end": v(-1708.15, 0) * mm, "construction": true});
            skPoint(sketch, "E111.orphan", {"position": v(-876.3, -88.01) * mm});
            skPoint(sketch, "E112.orphan", {"position": v(876.3, -147.03) * mm});
            skLineSegment(sketch, "E113", {"start": v(-876.3, 0) * mm, "end": v(-1028.7, 0) * mm});
            skLineSegment(sketch, "E114", {"start": v(-1028.7, 0) * mm, "end": v(-1028.7, 25.4) * mm});
            skLineSegment(sketch, "E115", {"start": v(-1015.77, 25.4) * mm, "end": v(-909.32, 25.4) * mm});
            skLineSegment(sketch, "E116", {"start": v(-883.92, 50.8) * mm, "end": v(-883.92, 264.03) * mm});
            skLineSegment(sketch, "E117", {"start": v(-909.32, 289.43) * mm, "end": v(-1028.7, 289.43) * mm});
            skLineSegment(sketch, "E118", {"start": v(-1028.7, 289.43) * mm, "end": v(-1028.7, 304.8) * mm});
            skLineSegment(sketch, "E119", {"start": v(-1028.7, 304.8) * mm, "end": v(-876.3, 304.8) * mm});
            skPoint(sketch, "E120.visualSharp", {"position": v(-883.92, 289.43) * mm});
            skArc(sketch, "E120.filletArc", {"start": v(-883.92, 264.03) * mm, "mid": v(-891.36, 282) * mm, "end": v(-909.32, 289.43) * mm});
            skPoint(sketch, "E121.visualSharp", {"position": v(-883.92, 25.4) * mm});
            skArc(sketch, "E121.filletArc", {"start": v(-909.32, 25.4) * mm, "mid": v(-891.36, 32.84) * mm, "end": v(-883.92, 50.8) * mm});
            skLineSegment(sketch, "E122.MirrorCS", {"start": v(-723.9, 289.43) * mm, "end": v(-723.9, 304.8) * mm});
            skLineSegment(sketch, "E123.MirrorCS", {"start": v(-723.9, 0) * mm, "end": v(-723.9, 25.4) * mm});
            skArc(sketch, "E124.MirrorCS", {"start": v(-843.28, 25.4) * mm, "mid": v(-861.24, 32.84) * mm, "end": v(-868.68, 50.8) * mm});
            skArc(sketch, "E125.MirrorCS", {"start": v(-868.68, 264.03) * mm, "mid": v(-861.24, 282) * mm, "end": v(-843.28, 289.43) * mm});
            skLineSegment(sketch, "E126.MirrorCS", {"start": v(-736.83, 25.4) * mm, "end": v(-843.28, 25.4) * mm});
            skLineSegment(sketch, "E127.MirrorCS", {"start": v(-868.68, 50.8) * mm, "end": v(-868.68, 264.03) * mm});
            skLineSegment(sketch, "E128.MirrorCS", {"start": v(-876.3, 0) * mm, "end": v(-723.9, 0) * mm});
            skLineSegment(sketch, "E129.MirrorCS", {"start": v(-843.28, 289.43) * mm, "end": v(-723.9, 289.43) * mm});
            skPoint(sketch, "E130.MirrorP", {"position": v(-868.68, 25.4) * mm});
            skLineSegment(sketch, "E131.MirrorCS", {"start": v(-723.9, 304.8) * mm, "end": v(-876.3, 304.8) * mm});
            skPoint(sketch, "E132.MirrorP", {"position": v(-868.68, 289.43) * mm});
            skLineSegment(sketch, "E133", {"start": v(-876.3, 709.43) * mm, "end": v(876.3, 709.43) * mm, "construction": true});
            skLineSegment(sketch, "E134", {"start": v(0, 709.43) * mm, "end": v(0, 444.83) * mm, "construction": true});
            skArc(sketch, "E135.MirrorCS", {"start": v(909.32, 25.4) * mm, "mid": v(891.36, 32.84) * mm, "end": v(883.92, 50.8) * mm});
            skArc(sketch, "E136.MirrorCS", {"start": v(868.68, 264.03) * mm, "mid": v(861.24, 282) * mm, "end": v(843.28, 289.43) * mm});
            skArc(sketch, "E137.MirrorCS", {"start": v(843.28, 25.4) * mm, "mid": v(861.24, 32.84) * mm, "end": v(868.68, 50.8) * mm});
            skArc(sketch, "E138.MirrorCS", {"start": v(883.92, 264.03) * mm, "mid": v(891.36, 282) * mm, "end": v(909.32, 289.43) * mm});
            skLineSegment(sketch, "E139.MirrorCS", {"start": v(723.9, 0) * mm, "end": v(723.9, 25.4) * mm});
            skLineSegment(sketch, "E140.MirrorCS", {"start": v(723.9, 289.43) * mm, "end": v(723.9, 304.8) * mm});
            skLineSegment(sketch, "E141.MirrorCS", {"start": v(1028.7, 289.43) * mm, "end": v(1028.7, 304.8) * mm});
            skLineSegment(sketch, "E142.MirrorCS", {"start": v(1028.7, 0) * mm, "end": v(1028.7, 25.4) * mm});
            skPoint(sketch, "E143.MirrorP", {"position": v(876.3, 25.4) * mm});
            skPoint(sketch, "E144.MirrorP", {"position": v(876.3, -88.01) * mm});
            skPoint(sketch, "E145.MirrorP", {"position": v(868.68, 25.4) * mm});
            skPoint(sketch, "E146.MirrorP", {"position": v(883.92, 289.43) * mm});
            skLineSegment(sketch, "E147.MirrorCS", {"start": v(876.3, 0) * mm, "end": v(723.9, 0) * mm});
            skLineSegment(sketch, "E148.MirrorCS", {"start": v(723.9, 304.8) * mm, "end": v(876.3, 304.8) * mm});
            skPoint(sketch, "E149.MirrorP", {"position": v(883.92, 25.4) * mm});
            skLineSegment(sketch, "E150.MirrorCS", {"start": v(1015.77, 25.4) * mm, "end": v(909.32, 25.4) * mm});
            skPoint(sketch, "E151.MirrorP", {"position": v(868.68, 289.43) * mm});
            skLineSegment(sketch, "E152.MirrorCS", {"start": v(736.83, 25.4) * mm, "end": v(843.28, 25.4) * mm});
            skLineSegment(sketch, "E153.MirrorCS", {"start": v(883.92, 50.8) * mm, "end": v(883.92, 264.03) * mm});
            skLineSegment(sketch, "E154.MirrorCS", {"start": v(876.3, 0) * mm, "end": v(1028.7, 0) * mm});
            skLineSegment(sketch, "E155.MirrorCS", {"start": v(909.32, 289.43) * mm, "end": v(1028.7, 289.43) * mm});
            skLineSegment(sketch, "E156.MirrorCS", {"start": v(868.68, 50.8) * mm, "end": v(868.68, 264.03) * mm});
            skLineSegment(sketch, "E157.MirrorCS", {"start": v(843.28, 289.43) * mm, "end": v(723.9, 289.43) * mm});
            skLineSegment(sketch, "E158.MirrorCS", {"start": v(1028.7, 304.8) * mm, "end": v(876.3, 304.8) * mm});
            skSolve(sketch);
        }
        {
            var Q0;
            Q0=qCreatedBy(makeId("Front.planeOp"),FACE);
            cPlane(context, id + "F28", {"entities" : qUnion([Q0]), "cplaneType" : CPlaneType.OFFSET, "offset" : 1193.8 * mm, "oppositeDirection" : true, "width" : 152.4 * mm, "height" : 152.4 * mm});
        }
        {
            var Q0;
            Q0=makeQuery(id+"F27.imprint","IMPRINT",FACE,{"disambiguationData":[TD([[makeQuery(id+"F27.imprint","IMPRINT",EDGE,{"derivedFrom":sQuery(id+"F27.wireOp",EDGE,"E116")}),-1.0]])]});
            var Q1;
            Q1=makeQuery(id+"F27.imprint","IMPRINT",FACE,{"disambiguationData":[TD([[makeQuery(id+"F27.imprint","IMPRINT",EDGE,{"derivedFrom":sQuery(id+"F27.wireOp",EDGE,"E113")}),-1.0]])]});
            var Q2;
            Q2=qCreatedBy(id+"F28.planeOp",FACE);
            extrude(context, id + "F29", {"entities" : qUnion([Q0, Q1]), "endBound" : BoundingType.UP_TO_SURFACE, "endBoundEntityFace" : qUnion([Q2]), "depth" : 25.4 * mm});
        }
        {
            var Q0;
            Q0=makeQuery(id+"F29.opExtrude","SWEPT_BODY",BODY,{"disambiguationData":[OSD([sQuery(id+"F0.wireOp",EDGE,"E0.bottom"),sQuery(id+"F0.wireOp",EDGE,"E0.top"),sQuery(id+"F0.wireOp",EDGE,"E0.left"),sQuery(id+"F0.wireOp",EDGE,"E0.right"),sQuery(id+"F2.wireOp",EDGE,"E1.top"),sQuery(id+"F27.wireOp",EDGE,"E113"),sQuery(id+"F27.wireOp",EDGE,"E114"),sQuery(id+"F27.wireOp",EDGE,"E115"),sQuery(id+"F27.wireOp",EDGE,"E116"),sQuery(id+"F27.wireOp",EDGE,"E117"),sQuery(id+"F27.wireOp",EDGE,"E118"),sQuery(id+"F27.wireOp",EDGE,"E119"),sQuery(id+"F27.wireOp",EDGE,"E120.filletArc"),sQuery(id+"F27.wireOp",EDGE,"E121.filletArc"),sQuery(id+"F27.wireOp",EDGE,"E122.MirrorCS"),sQuery(id+"F27.wireOp",EDGE,"E123.MirrorCS"),sQuery(id+"F27.wireOp",EDGE,"E124.MirrorCS"),sQuery(id+"F27.wireOp",EDGE,"E125.MirrorCS"),sQuery(id+"F27.wireOp",EDGE,"E126.MirrorCS"),sQuery(id+"F27.wireOp",EDGE,"E127.MirrorCS"),sQuery(id+"F27.wireOp",EDGE,"E128.MirrorCS"),sQuery(id+"F27.wireOp",EDGE,"E129.MirrorCS"),sQuery(id+"F27.wireOp",EDGE,"E131.MirrorCS")])]});
            var Q1;
            Q1=qCreatedBy(makeId("Right.planeOp"),FACE);
            mirror(context, id + "F30", {"entities" : qUnion([Q0]), "mirrorPlane" : qUnion([Q1])});
        }
        {
            var Q0;
            Q0=makeQuery(id+"F1.opExtrude","SWEPT_BODY",BODY,{"disambiguationData":[OSD([sQuery(id+"F0.wireOp",EDGE,"E0.bottom"),sQuery(id+"F0.wireOp",EDGE,"E0.top"),sQuery(id+"F0.wireOp",EDGE,"E0.left"),sQuery(id+"F0.wireOp",EDGE,"E0.right")])]});
            var Q1;
            Q1=makeQuery(id+"F29.opExtrude","SWEPT_BODY",BODY,{"disambiguationData":[OSD([sQuery(id+"F0.wireOp",EDGE,"E0.bottom"),sQuery(id+"F0.wireOp",EDGE,"E0.top"),sQuery(id+"F0.wireOp",EDGE,"E0.left"),sQuery(id+"F0.wireOp",EDGE,"E0.right"),sQuery(id+"F2.wireOp",EDGE,"E1.top"),sQuery(id+"F27.wireOp",EDGE,"E113"),sQuery(id+"F27.wireOp",EDGE,"E114"),sQuery(id+"F27.wireOp",EDGE,"E115"),sQuery(id+"F27.wireOp",EDGE,"E116"),sQuery(id+"F27.wireOp",EDGE,"E117"),sQuery(id+"F27.wireOp",EDGE,"E118"),sQuery(id+"F27.wireOp",EDGE,"E119"),sQuery(id+"F27.wireOp",EDGE,"E120.filletArc"),sQuery(id+"F27.wireOp",EDGE,"E121.filletArc"),sQuery(id+"F27.wireOp",EDGE,"E122.MirrorCS"),sQuery(id+"F27.wireOp",EDGE,"E123.MirrorCS"),sQuery(id+"F27.wireOp",EDGE,"E124.MirrorCS"),sQuery(id+"F27.wireOp",EDGE,"E125.MirrorCS"),sQuery(id+"F27.wireOp",EDGE,"E126.MirrorCS"),sQuery(id+"F27.wireOp",EDGE,"E127.MirrorCS"),sQuery(id+"F27.wireOp",EDGE,"E128.MirrorCS"),sQuery(id+"F27.wireOp",EDGE,"E129.MirrorCS"),sQuery(id+"F27.wireOp",EDGE,"E131.MirrorCS")])]});
            var Q2;
            Q2=makeQuery(id+"F30.opPattern","COPY",BODY,{"derivedFrom":makeQuery(id+"F29.opExtrude","SWEPT_BODY",BODY,{"disambiguationData":[OSD([sQuery(id+"F0.wireOp",EDGE,"E0.bottom"),sQuery(id+"F0.wireOp",EDGE,"E0.top"),sQuery(id+"F0.wireOp",EDGE,"E0.left"),sQuery(id+"F0.wireOp",EDGE,"E0.right"),sQuery(id+"F2.wireOp",EDGE,"E1.top"),sQuery(id+"F27.wireOp",EDGE,"E113"),sQuery(id+"F27.wireOp",EDGE,"E114"),sQuery(id+"F27.wireOp",EDGE,"E115"),sQuery(id+"F27.wireOp",EDGE,"E116"),sQuery(id+"F27.wireOp",EDGE,"E117"),sQuery(id+"F27.wireOp",EDGE,"E118"),sQuery(id+"F27.wireOp",EDGE,"E119"),sQuery(id+"F27.wireOp",EDGE,"E120.filletArc"),sQuery(id+"F27.wireOp",EDGE,"E121.filletArc"),sQuery(id+"F27.wireOp",EDGE,"E122.MirrorCS"),sQuery(id+"F27.wireOp",EDGE,"E123.MirrorCS"),sQuery(id+"F27.wireOp",EDGE,"E124.MirrorCS"),sQuery(id+"F27.wireOp",EDGE,"E125.MirrorCS"),sQuery(id+"F27.wireOp",EDGE,"E126.MirrorCS"),sQuery(id+"F27.wireOp",EDGE,"E127.MirrorCS"),sQuery(id+"F27.wireOp",EDGE,"E128.MirrorCS"),sQuery(id+"F27.wireOp",EDGE,"E129.MirrorCS"),sQuery(id+"F27.wireOp",EDGE,"E131.MirrorCS")])]}),"instanceName":"1"});
            var Q3;
            Q3=qCreatedBy(id+"F28.planeOp",FACE);
            mirror(context, id + "F31", {"entities" : qUnion([Q0, Q1, Q2]), "mirrorPlane" : qUnion([Q3])});
        }
    });
